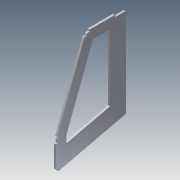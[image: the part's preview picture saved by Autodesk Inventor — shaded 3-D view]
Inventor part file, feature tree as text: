
AUTODESK INVENTOR PART (.ipt)
format: ipt  version: 2014 (Build 180170000, 170)  size: 190,976 bytes
history: native  units: mm
features: extrude x7, sketch x7, fillet x3
ambient origin geometry x8: Origin, YZ Plane, XZ Plane, XY Plane, X Axis, Y Axis, Z Axis, Center Point
bodies: Solid1 (feature_tree)
feature tree (17):
  extrude  "Extrusion1"  Depth=211.0mm
  extrude  "Extrusion2"  Depth=120.0mm
  extrude  "Extrusion3"  Depth=6.0mm
  extrude  "Extrusion6"  Depth=6.0mm
  fillet  "Fillet2"  Radius=8.1mm
  fillet  "Fillet3"  Radius=8.1mm
  extrude  "Extrusion4"  Depth=3.0mm
  extrude  "Extrusion7"  Depth=50.0mm
  extrude  "Extrusion8"  Depth=25.0mm
  fillet  "Fillet4"  Radius=4.0mm
  sketch  "Sketch1"  dims[d0=325.0mm d1=211.0mm]
  sketch  "Sketch2"  dims[d2=85.0mm d3=120.0mm]
  sketch  "Sketch3"  dims[d4=6.0mm d5=0.0mm d6=6.0mm]
  sketch  "Sketch4"  dims[d9=6.0mm d10=0.0mm d12=6.0mm d13=8.1mm d17=8.1mm]
  sketch  "Sketch6"  dims[d20=6.0mm d21=0.0mm d22=3.0mm]
  sketch  "Sketch7"  dims[d23=2.0mm d24=50.0mm]
  sketch  "Sketch8"  dims[d26=25.0mm d27=25.0mm d29=4.0mm d30=0.0mm d33=240.0mm d34=91.0mm d35=6.0mm d36=8.1mm d38=25.0mm d39=50.0mm d40=10.0mm d41=0.0mm d42=10.0mm d43=0.0mm d44=10.0mm d45=6.0mm d46=0.0mm d47=8.1mm d48=8.1mm d49=2.0mm]
